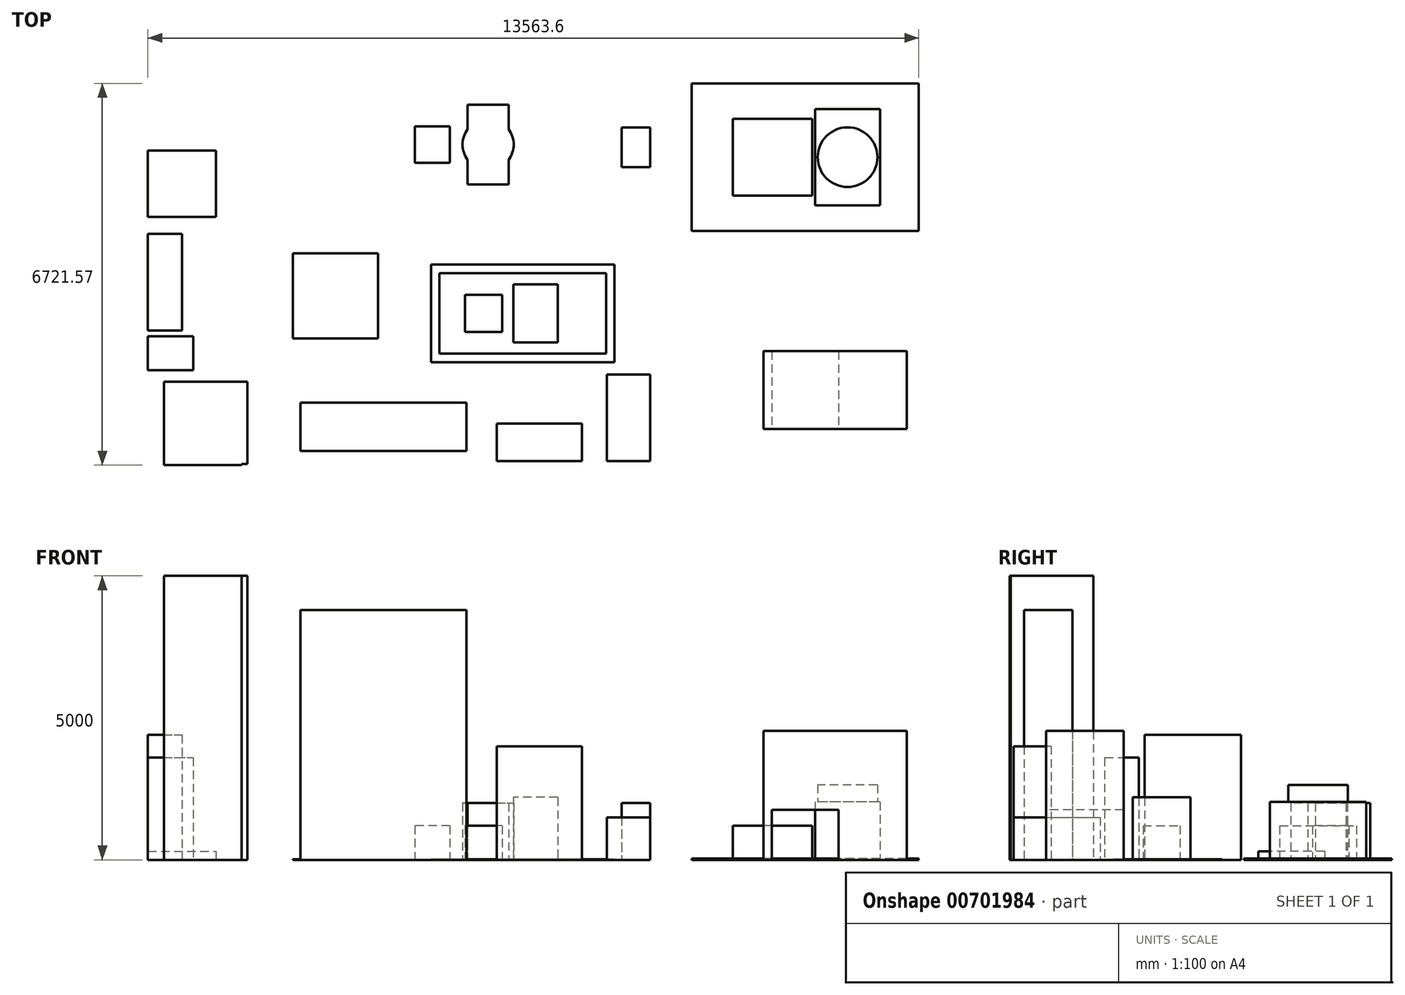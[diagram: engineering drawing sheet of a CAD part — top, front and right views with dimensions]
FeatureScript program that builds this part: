
annotation { "Feature Type Name" : "Feature", "Feature Type Description" : "" }
export const myFeature = defineFeature(function(context is Context, id is Id, definition is map)
    precondition{}
    {
        {
            var Q0;
            Q0=qCreatedBy(makeId("Top.planeOp"),FACE);
            var sketch = newSketch(context, id + "F0", { "sketchPlane" : qUnion([Q0])});
            skLineSegment(sketch, "E0.bottom", {"start": v(1700, 0) * mm, "end": v(8935, 0) * mm});
            skLineSegment(sketch, "E0.top", {"start": v(2000, 6825) * mm, "end": v(8935, 6825) * mm});
            skLineSegment(sketch, "E0.left", {"start": v(0, 0) * mm, "end": v(0, 6825) * mm});
            skLineSegment(sketch, "E0.right", {"start": v(8935, 0) * mm, "end": v(8935, 6825) * mm});
            skLineSegment(sketch, "E1.1", {"start": v(-100, 0) * mm, "end": v(-100, 6805) * mm});
            skLineSegment(sketch, "E1.3", {"start": v(9035, -100) * mm, "end": v(9035, 6925) * mm});
            skLineSegment(sketch, "E2", {"start": v(0, 6825) * mm, "end": v(2000, 7225) * mm});
            skLineSegment(sketch, "E3", {"start": v(2000, 7225) * mm, "end": v(2000, 6825) * mm});
            skLineSegment(sketch, "E4", {"start": v(1700, 0) * mm, "end": v(1700, -450) * mm});
            skLineSegment(sketch, "E5", {"start": v(1700, -450) * mm, "end": v(0, -450) * mm});
            skLineSegment(sketch, "E6", {"start": v(0, -450) * mm, "end": v(0, 0) * mm});
            skLineSegment(sketch, "E7.trimOffspring", {"start": v(1800, -100) * mm, "end": v(9035, -100) * mm});
            skLineSegment(sketch, "E8.0", {"start": v(-100, -550) * mm, "end": v(-100, 0) * mm});
            skLineSegment(sketch, "E8.1", {"start": v(1800, -550) * mm, "end": v(-100, -550) * mm});
            skLineSegment(sketch, "E8.2", {"start": v(1800, -100) * mm, "end": v(1800, -550) * mm});
            skLineSegment(sketch, "E9.trimOffspring", {"start": v(2000, 6925) * mm, "end": v(9035, 6925) * mm});
            skLineSegment(sketch, "E10", {"start": v(-100, 6805) * mm, "end": v(0, 6825) * mm});
            skSolve(sketch);
        }
        {
            var Q0;
            {var subQ1=sQuery(id+"F0.wireOp",EDGE,"E0.bottom");Q0=makeQuery(id+"F0.imprint","IMPRINT",FACE,{"disambiguationData":[TD([[makeQuery(id+"F0.imprint","IMPRINT",EDGE,{"derivedFrom":subQ1}),1.0]])]});}
            var sketch = newSketch(context, id + "F1", { "sketchPlane" : qUnion([Q0])});
            skLineSegment(sketch, "E11.bottom", {"start": v(5675, 6325) * mm, "end": v(6395, 6325) * mm});
            skLineSegment(sketch, "E11.top", {"start": v(5675, 4925) * mm, "end": v(6395, 4925) * mm});
            skLineSegment(sketch, "E11.left", {"start": v(5675, 6325) * mm, "end": v(5675, 4925) * mm});
            skLineSegment(sketch, "E11.right", {"start": v(6395, 6325) * mm, "end": v(6395, 4925) * mm});
            skLineSegment(sketch, "E12.bottom", {"start": v(5365, 5945) * mm, "end": v(4745, 5945) * mm});
            skLineSegment(sketch, "E12.top", {"start": v(5365, 5305) * mm, "end": v(4745, 5305) * mm});
            skLineSegment(sketch, "E12.left", {"start": v(5365, 5945) * mm, "end": v(5365, 5305) * mm});
            skLineSegment(sketch, "E12.right", {"start": v(4745, 5945) * mm, "end": v(4745, 5305) * mm});
            skCircle(sketch, "E13", {"center": v(6035, 5625) * mm, "radius": 450 * mm});
            skPoint(sketch, "E13.centerSnap0", {"position": v(6395, 5625) * mm});
            skPoint(sketch, "E13.centerSnap1", {"position": v(6035, 4925) * mm});
            skLineSegment(sketch, "E14.bottom", {"start": v(8260, 3512) * mm, "end": v(5030, 3512) * mm});
            skLineSegment(sketch, "E14.top", {"start": v(8260, 1792) * mm, "end": v(5030, 1792) * mm});
            skLineSegment(sketch, "E14.left", {"start": v(8260, 3512) * mm, "end": v(8260, 1792) * mm});
            skLineSegment(sketch, "E14.right", {"start": v(5030, 3512) * mm, "end": v(5030, 1792) * mm});
            skLineSegment(sketch, "E15.bottom", {"start": v(330, -19) * mm, "end": v(1800, -19) * mm});
            skLineSegment(sketch, "E15.top", {"start": v(330, 1451) * mm, "end": v(1800, 1451) * mm});
            skLineSegment(sketch, "E15.left", {"start": v(330, -19) * mm, "end": v(330, 1451) * mm});
            skLineSegment(sketch, "E15.right", {"start": v(1800, -19) * mm, "end": v(1800, 1451) * mm});
            skLineSegment(sketch, "E16.bottom", {"start": v(2731, 1080) * mm, "end": v(5651, 1080) * mm});
            skLineSegment(sketch, "E16.top", {"start": v(2731, 230) * mm, "end": v(5651, 230) * mm});
            skLineSegment(sketch, "E16.left", {"start": v(2731, 1080) * mm, "end": v(2731, 230) * mm});
            skLineSegment(sketch, "E16.right", {"start": v(5651, 1080) * mm, "end": v(5651, 230) * mm});
            skLineSegment(sketch, "E17.bottom", {"start": v(6189, 710) * mm, "end": v(7689, 710) * mm});
            skLineSegment(sketch, "E17.top", {"start": v(6189, 50) * mm, "end": v(7689, 50) * mm});
            skLineSegment(sketch, "E17.left", {"start": v(6189, 710) * mm, "end": v(6189, 50) * mm});
            skLineSegment(sketch, "E17.right", {"start": v(7689, 710) * mm, "end": v(7689, 50) * mm});
            skLineSegment(sketch, "E18.bottom", {"start": v(8885, 50) * mm, "end": v(8125, 50) * mm});
            skLineSegment(sketch, "E18.top", {"start": v(8885, 1575) * mm, "end": v(8125, 1575) * mm});
            skLineSegment(sketch, "E18.left", {"start": v(8885, 50) * mm, "end": v(8885, 1575) * mm});
            skLineSegment(sketch, "E18.right", {"start": v(8125, 50) * mm, "end": v(8125, 1575) * mm});
            skLineSegment(sketch, "E19.bottom", {"start": v(8885, 5925) * mm, "end": v(8385, 5925) * mm});
            skLineSegment(sketch, "E19.top", {"start": v(8885, 5225) * mm, "end": v(8385, 5225) * mm});
            skLineSegment(sketch, "E19.left", {"start": v(8885, 5925) * mm, "end": v(8885, 5225) * mm});
            skLineSegment(sketch, "E19.right", {"start": v(8385, 5925) * mm, "end": v(8385, 5225) * mm});
            skLineSegment(sketch, "E20.bottom", {"start": v(50, 1651) * mm, "end": v(850, 1651) * mm});
            skLineSegment(sketch, "E20.top", {"start": v(50, 2251) * mm, "end": v(850, 2251) * mm});
            skLineSegment(sketch, "E20.left", {"start": v(50, 1651) * mm, "end": v(50, 2251) * mm});
            skLineSegment(sketch, "E20.right", {"start": v(850, 1651) * mm, "end": v(850, 2251) * mm});
            skLineSegment(sketch, "E21.bottom", {"start": v(50, 2351) * mm, "end": v(650, 2351) * mm});
            skLineSegment(sketch, "E21.top", {"start": v(50, 4051) * mm, "end": v(650, 4051) * mm});
            skLineSegment(sketch, "E21.left", {"start": v(50, 2351) * mm, "end": v(50, 4051) * mm});
            skLineSegment(sketch, "E21.right", {"start": v(650, 2351) * mm, "end": v(650, 4051) * mm});
            skLineSegment(sketch, "E22.bottom", {"start": v(50, 5521) * mm, "end": v(1250, 5521) * mm});
            skLineSegment(sketch, "E22.top", {"start": v(50, 4351) * mm, "end": v(1250, 4351) * mm});
            skLineSegment(sketch, "E22.left", {"start": v(50, 5521) * mm, "end": v(50, 4351) * mm});
            skLineSegment(sketch, "E22.right", {"start": v(1250, 5521) * mm, "end": v(1250, 4351) * mm});
            skLineSegment(sketch, "E23.bottom", {"start": v(2600, 2209) * mm, "end": v(4100, 2209) * mm});
            skLineSegment(sketch, "E23.top", {"start": v(2600, 3709) * mm, "end": v(4100, 3709) * mm});
            skLineSegment(sketch, "E23.left", {"start": v(2600, 2209) * mm, "end": v(2600, 3709) * mm});
            skLineSegment(sketch, "E23.right", {"start": v(4100, 2209) * mm, "end": v(4100, 3709) * mm});
            skPoint(sketch, "E24", {"position": v(5365, 5625) * mm});
            skLineSegment(sketch, "E25.0", {"start": v(8110, 3362) * mm, "end": v(5180, 3362) * mm});
            skLineSegment(sketch, "E25.1", {"start": v(8110, 3362) * mm, "end": v(8110, 1942) * mm});
            skLineSegment(sketch, "E25.2", {"start": v(8110, 1942) * mm, "end": v(5180, 1942) * mm});
            skLineSegment(sketch, "E25.3", {"start": v(5180, 3362) * mm, "end": v(5180, 1942) * mm});
            skLineSegment(sketch, "E26.bottom", {"start": v(7260, 2142) * mm, "end": v(6480, 2142) * mm});
            skLineSegment(sketch, "E26.top", {"start": v(7260, 3162) * mm, "end": v(6480, 3162) * mm});
            skLineSegment(sketch, "E26.left", {"start": v(7260, 2142) * mm, "end": v(7260, 3162) * mm});
            skLineSegment(sketch, "E26.right", {"start": v(6480, 2142) * mm, "end": v(6480, 3162) * mm});
            skPoint(sketch, "E26.middle", {"position": v(6870, 2652) * mm});
            skPoint(sketch, "E26.middle.positionSnap0", {"position": v(8110, 2652) * mm});
            skPoint(sketch, "E26.centerSnap0", {"position": v(8110, 2652) * mm});
            skLineSegment(sketch, "E27.bottom", {"start": v(6280, 2327) * mm, "end": v(5630, 2327) * mm});
            skLineSegment(sketch, "E27.top", {"start": v(6280, 2977) * mm, "end": v(5630, 2977) * mm});
            skLineSegment(sketch, "E27.left", {"start": v(6280, 2327) * mm, "end": v(6280, 2977) * mm});
            skLineSegment(sketch, "E27.right", {"start": v(5630, 2327) * mm, "end": v(5630, 2977) * mm});
            skPoint(sketch, "E27.middle", {"position": v(5955, 2652) * mm});
            skSolve(sketch);
        }
        {
            var Q0;
            {var subQ1=sQuery(id+"F1.wireOp",EDGE,"E15.top");Q0=makeQuery(id+"F1.imprint","IMPRINT",FACE,{"disambiguationData":[TD([[makeQuery(id+"F1.imprint","IMPRINT",EDGE,{"derivedFrom":subQ1}),-1.0]])]});}
            extrude(context, id + "F2", {"entities" : qUnion([Q0]), "depth" : 5000 * mm, "offsetDistance" : 25 * mm});
        }
        {
            var Q0;
            Q0=makeQuery(id+"F1.imprint","IMPRINT",FACE,{"disambiguationData":[TD([[makeQuery(id+"F1.imprint","IMPRINT",EDGE,{"derivedFrom":sQuery(id+"F1.wireOp",EDGE,"E16.bottom")}),-1.0]])]});
            extrude(context, id + "F3", {"entities" : qUnion([Q0]), "depth" : 4400 * mm, "offsetDistance" : 25 * mm});
        }
        {
            var Q0;
            Q0=makeQuery(id+"F1.imprint","IMPRINT",FACE,{"disambiguationData":[TD([[makeQuery(id+"F1.imprint","IMPRINT",EDGE,{"derivedFrom":sQuery(id+"F1.wireOp",EDGE,"E17.bottom")}),-1.0]])]});
            extrude(context, id + "F4", {"entities" : qUnion([Q0]), "depth" : 2000 * mm, "offsetDistance" : 25 * mm});
        }
        {
            var Q0;
            Q0=makeQuery(id+"F1.imprint","IMPRINT",FACE,{"disambiguationData":[TD([[makeQuery(id+"F1.imprint","IMPRINT",EDGE,{"derivedFrom":sQuery(id+"F1.wireOp",EDGE,"E26.bottom")}),-1.0]])]});
            extrude(context, id + "F5", {"entities" : qUnion([Q0]), "depth" : 1100 * mm, "offsetDistance" : 25 * mm});
        }
        {
            var Q0;
            Q0=makeQuery(id+"F1.imprint","IMPRINT",FACE,{"disambiguationData":[TD([[makeQuery(id+"F1.imprint","IMPRINT",EDGE,{"derivedFrom":sQuery(id+"F1.wireOp",EDGE,"E18.bottom")}),-1.0]])]});
            extrude(context, id + "F6", {"entities" : qUnion([Q0]), "depth" : 750 * mm, "offsetDistance" : 25 * mm});
        }
        {
            var Q0;
            {var subQ0=sQuery(id+"F1.wireOp",EDGE,"E13");var subQ1=sQuery(id+"F1.wireOp",EDGE,"E11.left");var subQ2=makeQuery(id+"F1.imprint","INTERSECT",VERTEX,{"disambiguationData":[OD(0.0)],"derivedFrom":[subQ1,subQ0]});Q0=makeQuery(id+"F1.imprint","IMPRINT",FACE,{"disambiguationData":[TD([[makeQuery(id+"F1.imprint","IMPRINT",EDGE,{"disambiguationData":[TD([[subQ2,-1.0]])],"derivedFrom":subQ1}),1.0]])]});}
            var Q1;
            {var subQ0=sQuery(id+"F1.wireOp",EDGE,"E11.top");Q1=makeQuery(id+"F1.imprint","IMPRINT",FACE,{"disambiguationData":[TD([[makeQuery(id+"F1.imprint","IMPRINT",EDGE,{"derivedFrom":subQ0}),1.0]])]});}
            var Q2;
            {var subQ0=sQuery(id+"F1.wireOp",EDGE,"E11.bottom");Q2=makeQuery(id+"F1.imprint","IMPRINT",FACE,{"disambiguationData":[TD([[makeQuery(id+"F1.imprint","IMPRINT",EDGE,{"derivedFrom":subQ0}),-1.0]])]});}
            var Q3;
            {var subQ0=sQuery(id+"F1.wireOp",EDGE,"E13");var subQ1=sQuery(id+"F1.wireOp",EDGE,"E11.right");var subQ2=makeQuery(id+"F1.imprint","INTERSECT",VERTEX,{"disambiguationData":[OD(0.0)],"derivedFrom":[subQ1,subQ0]});Q3=makeQuery(id+"F1.imprint","IMPRINT",FACE,{"disambiguationData":[TD([[makeQuery(id+"F1.imprint","IMPRINT",EDGE,{"disambiguationData":[TD([[subQ2,-1.0]])],"derivedFrom":subQ1}),1.0]])]});}
            var Q4;
            {var subQ0=sQuery(id+"F1.wireOp",EDGE,"E13");var subQ1=sQuery(id+"F1.wireOp",EDGE,"E11.left");var subQ2=makeQuery(id+"F1.imprint","INTERSECT",VERTEX,{"disambiguationData":[OD(0.0)],"derivedFrom":[subQ1,subQ0]});Q4=makeQuery(id+"F1.imprint","IMPRINT",FACE,{"disambiguationData":[TD([[makeQuery(id+"F1.imprint","IMPRINT",EDGE,{"disambiguationData":[TD([[subQ2,-1.0]])],"derivedFrom":subQ1}),-1.0]])]});}
            extrude(context, id + "F7", {"entities" : qUnion([Q0, Q1, Q2, Q3, Q4]), "depth" : 1000 * mm, "offsetDistance" : 25 * mm});
        }
        {
            var Q0;
            Q0=makeQuery(id+"F1.imprint","IMPRINT",FACE,{"disambiguationData":[TD([[makeQuery(id+"F1.imprint","IMPRINT",EDGE,{"derivedFrom":sQuery(id+"F1.wireOp",EDGE,"E19.bottom")}),1.0]])]});
            extrude(context, id + "F8", {"entities" : qUnion([Q0]), "depth" : 1000 * mm, "offsetDistance" : 25 * mm});
        }
        {
            var Q0;
            Q0=makeQuery(id+"F1.imprint","IMPRINT",FACE,{"disambiguationData":[TD([[makeQuery(id+"F1.imprint","IMPRINT",EDGE,{"derivedFrom":sQuery(id+"F1.wireOp",EDGE,"E12.bottom")}),1.0]])]});
            extrude(context, id + "F9", {"entities" : qUnion([Q0]), "depth" : 600 * mm, "offsetDistance" : 25 * mm});
        }
        {
            var Q0;
            Q0=makeQuery(id+"F1.imprint","IMPRINT",FACE,{"disambiguationData":[TD([[makeQuery(id+"F1.imprint","IMPRINT",EDGE,{"derivedFrom":sQuery(id+"F1.wireOp",EDGE,"E21.bottom")}),1.0]])]});
            extrude(context, id + "F10", {"entities" : qUnion([Q0]), "depth" : 2200 * mm, "offsetDistance" : 25 * mm});
        }
        {
            var Q0;
            Q0=makeQuery(id+"F1.imprint","IMPRINT",FACE,{"disambiguationData":[TD([[makeQuery(id+"F1.imprint","IMPRINT",EDGE,{"derivedFrom":sQuery(id+"F1.wireOp",EDGE,"E20.bottom")}),1.0]])]});
            extrude(context, id + "F11", {"entities" : qUnion([Q0]), "depth" : 1800 * mm, "offsetDistance" : 25 * mm});
        }
        {
            var Q0;
            Q0=makeQuery(id+"F1.imprint","IMPRINT",FACE,{"disambiguationData":[TD([[makeQuery(id+"F1.imprint","IMPRINT",EDGE,{"derivedFrom":sQuery(id+"F1.wireOp",EDGE,"E23.bottom")}),1.0]])]});
            extrude(context, id + "F12", {"entities" : qUnion([Q0]), "depth" : 10 * mm, "offsetDistance" : 25 * mm});
        }
        {
            var Q0;
            Q0=makeQuery(id+"F1.imprint","IMPRINT",FACE,{"disambiguationData":[TD([[makeQuery(id+"F1.imprint","IMPRINT",EDGE,{"derivedFrom":sQuery(id+"F1.wireOp",EDGE,"E22.bottom")}),-1.0]])]});
            extrude(context, id + "F13", {"entities" : qUnion([Q0]), "depth" : 150 * mm, "offsetDistance" : 25 * mm});
        }
        {
            var Q0;
            Q0=makeQuery(id+"F1.imprint","IMPRINT",FACE,{"disambiguationData":[TD([[makeQuery(id+"F1.imprint","IMPRINT",EDGE,{"derivedFrom":sQuery(id+"F1.wireOp",EDGE,"E14.bottom")}),1.0]])]});
            extrude(context, id + "F14", {"entities" : qUnion([Q0]), "depth" : 10 * mm, "offsetDistance" : 25 * mm});
        }
        {
            var Q0;
            Q0=makeQuery(id+"F1.imprint","IMPRINT",FACE,{"disambiguationData":[TD([[makeQuery(id+"F1.imprint","IMPRINT",EDGE,{"derivedFrom":sQuery(id+"F1.wireOp",EDGE,"E25.0")}),1.0]])]});
            extrude(context, id + "F15", {"entities" : qUnion([Q0]), "depth" : 10 * mm, "offsetDistance" : 25 * mm});
        }
        {
            var Q0;
            {var subQ4=sQuery(id+"F1.wireOp",EDGE,"E11.bottom");Q0=makeQuery(id+"F1.imprint","IMPRINT",FACE,{"disambiguationData":[TD([[makeQuery(id+"F1.imprint","IMPRINT",EDGE,{"derivedFrom":subQ4}),1.0]])]});}
            var sketch = newSketch(context, id + "F16", { "sketchPlane" : qUnion([Q0])});
            skLineSegment(sketch, "E28.bottom", {"start": v(13613.62, 4102.57) * mm, "end": v(9613.62, 4102.57) * mm});
            skLineSegment(sketch, "E28.top", {"start": v(13613.62, 6702.57) * mm, "end": v(9613.62, 6702.57) * mm});
            skLineSegment(sketch, "E28.left", {"start": v(13613.62, 4102.57) * mm, "end": v(13613.62, 6702.57) * mm});
            skLineSegment(sketch, "E28.right", {"start": v(9613.62, 4102.57) * mm, "end": v(9613.62, 6702.57) * mm});
            skPoint(sketch, "E28.middle", {"position": v(11613.62, 5402.57) * mm});
            skLineSegment(sketch, "E29.bottom", {"start": v(12928.4, 4556.07) * mm, "end": v(11790.4, 4556.07) * mm});
            skLineSegment(sketch, "E29.top", {"start": v(12928.4, 6249.07) * mm, "end": v(11790.4, 6249.07) * mm});
            skLineSegment(sketch, "E29.left", {"start": v(12928.4, 4556.07) * mm, "end": v(12928.4, 6249.07) * mm});
            skLineSegment(sketch, "E29.right", {"start": v(11790.4, 4556.07) * mm, "end": v(11790.4, 6249.07) * mm});
            skPoint(sketch, "E29.middle", {"position": v(12359.4, 5402.57) * mm});
            skPoint(sketch, "E29.middle.positionSnap0", {"position": v(13613.62, 5402.57) * mm});
            skPoint(sketch, "E29.centerSnap0", {"position": v(13613.62, 5402.57) * mm});
            skLineSegment(sketch, "E30.bottom", {"start": v(11740.4, 4727.57) * mm, "end": v(10340.4, 4727.57) * mm});
            skLineSegment(sketch, "E30.top", {"start": v(11740.4, 6077.57) * mm, "end": v(10340.4, 6077.57) * mm});
            skLineSegment(sketch, "E30.left", {"start": v(11740.4, 4727.57) * mm, "end": v(11740.4, 6077.57) * mm});
            skLineSegment(sketch, "E30.right", {"start": v(10340.4, 4727.57) * mm, "end": v(10340.4, 6077.57) * mm});
            skPoint(sketch, "E30.middle", {"position": v(11040.4, 5402.57) * mm});
            skCircle(sketch, "E31", {"center": v(12359.4, 5402.57) * mm, "radius": 525 * mm});
            skSolve(sketch);
        }
        {
            var Q0;
            Q0=makeQuery(id+"F16.imprint","IMPRINT",FACE,{"disambiguationData":[TD([[makeQuery(id+"F16.imprint","IMPRINT",EDGE,{"derivedFrom":sQuery(id+"F16.wireOp",EDGE,"E29.bottom")}),-1.0]])]});
            extrude(context, id + "F17", {"entities" : qUnion([Q0]), "depth" : 1020 * mm, "offsetDistance" : 25 * mm});
        }
        {
            var Q0;
            Q0=makeQuery(id+"F16.imprint","IMPRINT",FACE,{"disambiguationData":[TD([[makeQuery(id+"F16.imprint","IMPRINT",EDGE,{"derivedFrom":sQuery(id+"F16.wireOp",EDGE,"E31")}),1.0]])]});
            extrude(context, id + "F18", {"entities" : qUnion([Q0]), "operationType" : NewBodyOperationType.ADD, "depth" : 1320 * mm, "offsetDistance" : 25 * mm});
        }
        {
            var Q0;
            Q0=makeQuery(id+"F16.imprint","IMPRINT",FACE,{"disambiguationData":[TD([[makeQuery(id+"F16.imprint","IMPRINT",EDGE,{"derivedFrom":sQuery(id+"F16.wireOp",EDGE,"E30.bottom")}),-1.0]])]});
            extrude(context, id + "F19", {"entities" : qUnion([Q0]), "depth" : 600 * mm, "offsetDistance" : 25 * mm});
        }
        {
            var Q0;
            Q0=makeQuery(id+"F16.imprint","IMPRINT",FACE,{"disambiguationData":[TD([[makeQuery(id+"F16.imprint","IMPRINT",EDGE,{"derivedFrom":sQuery(id+"F16.wireOp",EDGE,"E28.bottom")}),-1.0]])]});
            extrude(context, id + "F20", {"entities" : qUnion([Q0]), "depth" : 25 * mm, "offsetDistance" : 25 * mm});
        }
        {
            var Q0;
            {var subQ4=sQuery(id+"F1.wireOp",EDGE,"E11.bottom");Q0=makeQuery(id+"F1.imprint","IMPRINT",FACE,{"disambiguationData":[TD([[makeQuery(id+"F1.imprint","IMPRINT",EDGE,{"derivedFrom":subQ4}),1.0]])]});}
            var sketch = newSketch(context, id + "F21", { "sketchPlane" : qUnion([Q0])});
            skLineSegment(sketch, "E32.bottom", {"start": v(13399.18, 617.87) * mm, "end": v(10879.18, 617.87) * mm});
            skLineSegment(sketch, "E32.top", {"start": v(13399.18, 1985.87) * mm, "end": v(10879.18, 1985.87) * mm});
            skLineSegment(sketch, "E32.left", {"start": v(13399.18, 617.87) * mm, "end": v(13399.18, 1985.87) * mm});
            skLineSegment(sketch, "E32.right", {"start": v(10879.18, 617.87) * mm, "end": v(10879.18, 1985.87) * mm});
            skPoint(sketch, "E32.middle", {"position": v(12139.18, 1301.87) * mm});
            skSolve(sketch);
        }
        {
            var Q0;
            Q0=makeQuery(id+"F21.imprint","IMPRINT",FACE,{"disambiguationData":[TD([[makeQuery(id+"F21.imprint","IMPRINT",EDGE,{"derivedFrom":sQuery(id+"F21.wireOp",EDGE,"E32.bottom")}),-1.0]])]});
            extrude(context, id + "F22", {"entities" : qUnion([Q0]), "depth" : 2269 * mm, "offsetDistance" : 25 * mm});
        }
        {
            var Q0;
            Q0=makeQuery(id+"F22.opExtrude","SWEPT_FACE",FACE,{"disambiguationData":[OSD([sQuery(id+"F21.wireOp",EDGE,"E32.bottom")])]});
            var sketch = newSketch(context, id + "F23", { "sketchPlane" : qUnion([Q0])});
            skLineSegment(sketch, "E33.bottom", {"start": v(11029.18, 0) * mm, "end": v(12199.18, 0) * mm});
            skLineSegment(sketch, "E33.top", {"start": v(11029.18, 879) * mm, "end": v(12199.18, 879) * mm});
            skLineSegment(sketch, "E33.left", {"start": v(11029.18, 0) * mm, "end": v(11029.18, 879) * mm});
            skLineSegment(sketch, "E33.right", {"start": v(12199.18, 0) * mm, "end": v(12199.18, 879) * mm});
            skSolve(sketch);
        }
        {
            var Q0;
            Q0=makeQuery(id+"F23.imprint","IMPRINT",FACE,{"disambiguationData":[TD([[makeQuery(id+"F23.imprint","IMPRINT",EDGE,{"derivedFrom":sQuery(id+"F23.wireOp",EDGE,"E33.bottom")}),-1.0]])]});
            extrude(context, id + "F24", {"entities" : qUnion([Q0]), "operationType" : NewBodyOperationType.REMOVE, "endBound" : BoundingType.UP_TO_NEXT, "oppositeDirection" : true, "depth" : 25 * mm, "offsetDistance" : 25 * mm});
        }
        {
            var Q0;
            Q0=makeQuery(id+"F1.imprint","IMPRINT",FACE,{"disambiguationData":[TD([[makeQuery(id+"F1.imprint","IMPRINT",EDGE,{"derivedFrom":sQuery(id+"F1.wireOp",EDGE,"E27.bottom")}),-1.0]])]});
            extrude(context, id + "F25", {"entities" : qUnion([Q0]), "operationType" : NewBodyOperationType.ADD, "depth" : 600 * mm, "offsetDistance" : 25 * mm});
        }
    });
